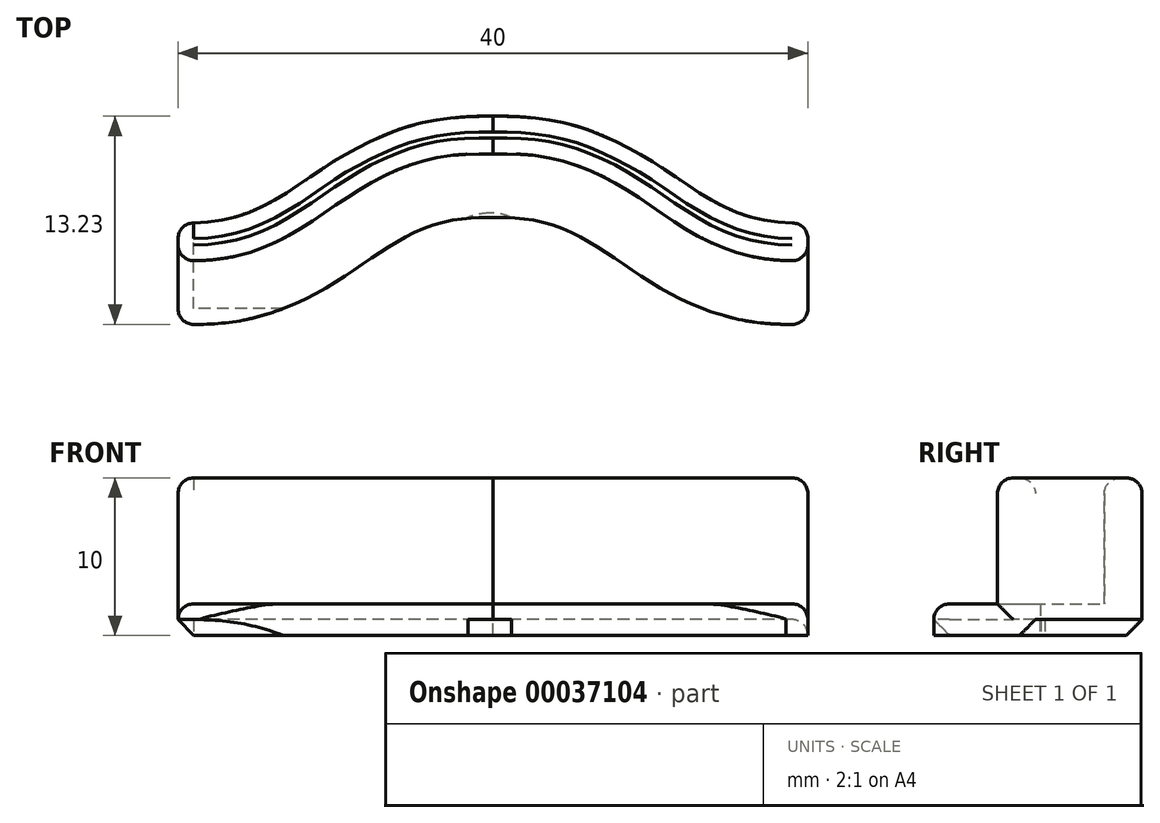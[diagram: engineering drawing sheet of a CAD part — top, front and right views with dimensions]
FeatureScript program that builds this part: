
annotation { "Feature Type Name" : "Feature", "Feature Type Description" : "" }
export const myFeature = defineFeature(function(context is Context, id is Id, definition is map)
    precondition{}
    {
        {
            var Q0;
            Q0=qCreatedBy(makeId("Top.planeOp"),FACE);
            var sketch = newSketch(context, id + "F0", { "sketchPlane" : qUnion([Q0]), "disableImprinting" : false});
            skLineSegment(sketch, "E0.bottom", {"start": v(-20, 0) * mm, "end": v(20, 0) * mm});
            skLineSegment(sketch, "E0.left", {"start": v(-20, 0) * mm, "end": v(-20, 6.45) * mm});
            skLineSegment(sketch, "E0.right", {"start": v(20, 0) * mm, "end": v(20, 6.45) * mm});
            skLineSegment(sketch, "E1", {"start": v(0, 0) * mm, "end": v(0, 13.22) * mm, "construction": true});
            skFitSpline(sketch, "E2", {"points": [v(-20, 2.4) * mm, v(0, 9.17) * mm], "startDerivative": vector(30.52, 0) * mm, "endDerivative": vector(27.9, 0) * mm});
            skFitSpline(sketch, "E3.MirrorCS", {"points": [v(20, 2.4) * mm, v(0, 9.17) * mm], "startDerivative": vector(-30.52, 0) * mm, "endDerivative": vector(-27.9, 0) * mm});
            skFitSpline(sketch, "E4.0", {"points": [v(20, 4.05) * mm, v(18.82, 4.05) * mm, v(16.78, 4.25) * mm, v(14.43, 4.95) * mm, v(12.46, 5.94) * mm, v(10.6, 7.15) * mm, v(8.63, 8.46) * mm, v(6.34, 9.7) * mm, v(3.54, 10.6) * mm, v(1.26, 10.82) * mm, v(0, 10.82) * mm]});
            skFitSpline(sketch, "E4.1", {"points": [v(-20, 4.05) * mm, v(-18.82, 4.05) * mm, v(-16.78, 4.25) * mm, v(-14.43, 4.95) * mm, v(-12.46, 5.94) * mm, v(-10.6, 7.15) * mm, v(-8.63, 8.46) * mm, v(-6.34, 9.7) * mm, v(-3.54, 10.6) * mm, v(-1.26, 10.82) * mm, v(0, 10.82) * mm]});
            skFitSpline(sketch, "E5.0", {"points": [v(20, 6.45) * mm, v(18.95, 6.45) * mm, v(17.22, 6.62) * mm, v(15.32, 7.19) * mm, v(13.69, 8) * mm, v(11.96, 9.12) * mm, v(10.24, 10.27) * mm, v(8.6, 11.2) * mm, v(6.75, 12.09) * mm, v(4.56, 12.79) * mm, v(2.06, 13.16) * mm, v(0.7, 13.22) * mm, v(0, 13.22) * mm]});
            skFitSpline(sketch, "E5.1", {"points": [v(-20, 6.45) * mm, v(-18.95, 6.45) * mm, v(-17.22, 6.62) * mm, v(-15.32, 7.19) * mm, v(-13.69, 8) * mm, v(-11.96, 9.12) * mm, v(-10.24, 10.27) * mm, v(-8.6, 11.2) * mm, v(-6.75, 12.09) * mm, v(-4.56, 12.79) * mm, v(-2.06, 13.16) * mm, v(-0.7, 13.22) * mm, v(0, 13.22) * mm]});
            skFitSpline(sketch, "E6.0", {"points": [v(20, 0) * mm, v(18.6, 0) * mm, v(16.05, 0.23) * mm, v(12.92, 1.16) * mm, v(10.38, 2.45) * mm, v(8.3, 3.8) * mm, v(6.5, 5.02) * mm, v(4.73, 5.95) * mm, v(2.74, 6.6) * mm, v(1.02, 6.77) * mm, v(0, 6.77) * mm]});
            skFitSpline(sketch, "E6.1", {"points": [v(-20, 0) * mm, v(-18.6, 0) * mm, v(-16.05, 0.23) * mm, v(-12.92, 1.16) * mm, v(-10.38, 2.45) * mm, v(-8.3, 3.8) * mm, v(-6.5, 5.02) * mm, v(-4.73, 5.95) * mm, v(-2.74, 6.6) * mm, v(-1.02, 6.77) * mm, v(0, 6.77) * mm]});
            skSolve(sketch);
        }
        {
            var Q0;
            Q0=makeQuery(id+"F0.imprint","IMPRINT",FACE,{"disambiguationData":[TD([[makeQuery(id+"F0.imprint","IMPRINT",EDGE,{"derivedFrom":sQuery(id+"F0.wireOp",EDGE,"E0.bottom")}),1.0]])]});
            var Q1;
            {var subQ3=sQuery(id+"F0.wireOp",EDGE,"E2");Q1=makeQuery(id+"F0.imprint","IMPRINT",FACE,{"disambiguationData":[TD([[makeQuery(id+"F0.imprint","IMPRINT",EDGE,{"derivedFrom":subQ3}),-1.0]])]});}
            var Q2;
            {var subQ3=sQuery(id+"F0.wireOp",EDGE,"E2");Q2=makeQuery(id+"F0.imprint","IMPRINT",FACE,{"disambiguationData":[TD([[makeQuery(id+"F0.imprint","IMPRINT",EDGE,{"derivedFrom":subQ3}),1.0]])]});}
            var Q3;
            {var subQ2=sQuery(id+"F0.wireOp",EDGE,"E4.0");Q3=makeQuery(id+"F0.imprint","IMPRINT",FACE,{"disambiguationData":[TD([[makeQuery(id+"F0.imprint","IMPRINT",EDGE,{"derivedFrom":subQ2}),-1.0]])]});}
            extrude(context, id + "F1", {"entities" : qUnion([Q0, Q1, Q2, Q3]), "depth" : 2 * mm});
        }
        {
            var Q0;
            {var subQ3=sQuery(id+"F0.wireOp",EDGE,"E2");Q0=makeQuery(id+"F0.imprint","IMPRINT",FACE,{"disambiguationData":[TD([[makeQuery(id+"F0.imprint","IMPRINT",EDGE,{"derivedFrom":subQ3}),-1.0]])]});}
            var Q1;
            {var subQ2=sQuery(id+"F0.wireOp",EDGE,"E4.0");Q1=makeQuery(id+"F0.imprint","IMPRINT",FACE,{"disambiguationData":[TD([[makeQuery(id+"F0.imprint","IMPRINT",EDGE,{"derivedFrom":subQ2}),-1.0]])]});}
            extrude(context, id + "F2", {"entities" : qUnion([Q0, Q1]), "operationType" : NewBodyOperationType.ADD, "depth" : 10 * mm});
        }
        {
            var Q0;
            Q0=makeQuery(id+"F2.opExtrude","CAP_EDGE",EDGE,{"disambiguationData":[OSD([sQuery(id+"F0.wireOp",EDGE,"E4.0")])],"isStart":false});
            var Q1;
            Q1=makeQuery(id+"F2.opExtrude","CAP_EDGE",EDGE,{"disambiguationData":[OSD([sQuery(id+"F0.wireOp",EDGE,"E4.1")])],"isStart":false});
            var Q2;
            Q2=makeQuery(id+"F2.opExtrude","CAP_EDGE",EDGE,{"disambiguationData":[OSD([sQuery(id+"F0.wireOp",EDGE,"E3.MirrorCS")])],"isStart":false});
            var Q3;
            Q3=makeQuery(id+"F2.opExtrude","SWEPT_EDGE",EDGE,{"disambiguationData":[OSD([sQuery(id+"F0.wireOp",EDGE,"E0.left"),sQuery(id+"F0.wireOp",EDGE,"E4.1")])]});
            var Q4;
            Q4=makeQuery(id+"F2.opExtrude","SWEPT_EDGE",EDGE,{"disambiguationData":[OSD([sQuery(id+"F0.wireOp",EDGE,"E0.left"),sQuery(id+"F0.wireOp",EDGE,"E2")])]});
            var Q5;
            Q5=makeQuery(id+"F2.opExtrude","SWEPT_EDGE",EDGE,{"disambiguationData":[OSD([sQuery(id+"F0.wireOp",EDGE,"E0.right"),sQuery(id+"F0.wireOp",EDGE,"E3.MirrorCS")])]});
            var Q6;
            Q6=makeQuery(id+"F2.opExtrude","SWEPT_EDGE",EDGE,{"disambiguationData":[OSD([sQuery(id+"F0.wireOp",EDGE,"E0.right"),sQuery(id+"F0.wireOp",EDGE,"E4.0")])]});
            var Q7;
            {var subQ0=sQuery(id+"F0.wireOp",EDGE,"E0.left");var subQ1=sQuery(id+"F0.wireOp",EDGE,"E5.1");Q7=makeQuery(id+"F2.boolean.opBoolean","MERGE",EDGE,{"derivedFrom":[makeQuery(id+"F1.opExtrude","SWEPT_EDGE",EDGE,{"disambiguationData":[OSD([subQ0,subQ1])]}),makeQuery(id+"F2.opExtrude","SWEPT_EDGE",EDGE,{"disambiguationData":[OSD([subQ0,subQ1])]})]});}
            var Q8;
            {var subQ0=sQuery(id+"F0.wireOp",EDGE,"E0.right");var subQ1=sQuery(id+"F0.wireOp",EDGE,"E5.0");Q8=makeQuery(id+"F2.boolean.opBoolean","MERGE",EDGE,{"derivedFrom":[makeQuery(id+"F1.opExtrude","SWEPT_EDGE",EDGE,{"disambiguationData":[OSD([subQ0,subQ1])]}),makeQuery(id+"F2.opExtrude","SWEPT_EDGE",EDGE,{"disambiguationData":[OSD([subQ0,subQ1])]})]});}
            var Q9;
            Q9=makeQuery(id+"F1.opExtrude","SWEPT_EDGE",EDGE,{"disambiguationData":[OSD([sQuery(id+"F0.wireOp",EDGE,"E0.bottom"),sQuery(id+"F0.wireOp",EDGE,"E0.left"),sQuery(id+"F0.wireOp",EDGE,"E6.1")])]});
            var Q10;
            Q10=makeQuery(id+"F1.opExtrude","SWEPT_EDGE",EDGE,{"disambiguationData":[OSD([sQuery(id+"F0.wireOp",EDGE,"E0.bottom"),sQuery(id+"F0.wireOp",EDGE,"E0.right"),sQuery(id+"F0.wireOp",EDGE,"E6.0")])]});
            var Q11;
            Q11=makeQuery(id+"F2.boolean.opBoolean","INTERSECT",EDGE,{"derivedFrom":[makeQuery(id+"F1.opExtrude","CAP_FACE",FACE,{"disambiguationData":[OSD([sQuery(id+"F0.wireOp",EDGE,"E0.bottom"),sQuery(id+"F0.wireOp",EDGE,"E0.left"),sQuery(id+"F0.wireOp",EDGE,"E0.right"),sQuery(id+"F0.wireOp",EDGE,"E5.0"),sQuery(id+"F0.wireOp",EDGE,"E5.1")])],"isStart":false}),makeQuery(id+"F2.opExtrude","SWEPT_FACE",FACE,{"disambiguationData":[OSD([sQuery(id+"F0.wireOp",EDGE,"E6.0")])]})]});
            var Q12;
            Q12=makeQuery(id+"F2.opExtrude","CAP_EDGE",EDGE,{"disambiguationData":[OSD([sQuery(id+"F0.wireOp",EDGE,"E6.1")])],"isStart":false});
            var Q13;
            Q13=makeQuery(id+"F2.opExtrude","CAP_EDGE",EDGE,{"disambiguationData":[OSD([sQuery(id+"F0.wireOp",EDGE,"E5.1")])],"isStart":false});
            var Q14;
            {var subQ0=sQuery(id+"F0.wireOp",EDGE,"E0.left");Q14=makeQuery(id+"F2.opExtrude","CAP_EDGE",EDGE,{"disambiguationData":[OSD([subQ0]),TDD([makeQuery(id+"F0.imprint","IMPRINT",EDGE,{"disambiguationData":[TD([[makeQuery(id+"F0.imprint","INTERSECT",VERTEX,{"derivedFrom":[subQ0,sQuery(id+"F0.wireOp",EDGE,"E5.1")]}),1.0]])],"derivedFrom":subQ0})])],"isStart":false});}
            var Q15;
            {var subQ0=sQuery(id+"F0.wireOp",EDGE,"E0.right");Q15=makeQuery(id+"F2.opExtrude","CAP_EDGE",EDGE,{"disambiguationData":[OSD([subQ0]),TDD([makeQuery(id+"F0.imprint","IMPRINT",EDGE,{"disambiguationData":[TD([[makeQuery(id+"F0.imprint","INTERSECT",VERTEX,{"derivedFrom":[subQ0,sQuery(id+"F0.wireOp",EDGE,"E5.0")]}),1.0]])],"derivedFrom":subQ0})])],"isStart":false});}
            var Q16;
            {var subQ0=sQuery(id+"F0.wireOp",EDGE,"E0.left");Q16=makeQuery(id+"F2.opExtrude","CAP_EDGE",EDGE,{"disambiguationData":[OSD([subQ0]),TDD([makeQuery(id+"F0.imprint","IMPRINT",EDGE,{"disambiguationData":[TD([[makeQuery(id+"F0.imprint","INTERSECT",VERTEX,{"derivedFrom":[subQ0,sQuery(id+"F0.wireOp",EDGE,"E2")]}),1.0]])],"derivedFrom":subQ0})])],"isStart":false});}
            var Q17;
            {var subQ0=sQuery(id+"F0.wireOp",EDGE,"E0.right");Q17=makeQuery(id+"F2.opExtrude","CAP_EDGE",EDGE,{"disambiguationData":[OSD([subQ0]),TDD([makeQuery(id+"F0.imprint","IMPRINT",EDGE,{"disambiguationData":[TD([[makeQuery(id+"F0.imprint","INTERSECT",VERTEX,{"derivedFrom":[subQ0,sQuery(id+"F0.wireOp",EDGE,"E3.MirrorCS")]}),1.0]])],"derivedFrom":subQ0})])],"isStart":false});}
            fillet(context, id + "F3", {"entities" : qUnion([Q0, Q1, Q2, Q3, Q4, Q5, Q6, Q7, Q8, Q9, Q10, Q11, Q12, Q13, Q14, Q15, Q16, Q17]), "radius" : 1 * mm, "tangentPropagation" : true, "allowEdgeOverflow" : false});
        }
        {
            var Q0;
            Q0=makeQuery(id+"F1.opExtrude","CAP_EDGE",EDGE,{"disambiguationData":[OSD([sQuery(id+"F0.wireOp",EDGE,"E0.bottom")])],"isStart":false});
            fillet(context, id + "F4", {"entities" : qUnion([Q0]), "radius" : 1 * mm, "tangentPropagation" : true, "allowEdgeOverflow" : false});
        }
        {
            var Q0;
            Q0=makeQuery(id+"F1.opExtrude","CAP_FACE",FACE,{"disambiguationData":[OSD([sQuery(id+"F0.wireOp",EDGE,"E0.bottom"),sQuery(id+"F0.wireOp",EDGE,"E0.left"),sQuery(id+"F0.wireOp",EDGE,"E0.right"),sQuery(id+"F0.wireOp",EDGE,"E5.0"),sQuery(id+"F0.wireOp",EDGE,"E5.1")])],"isStart":true});
            var sketch = newSketch(context, id + "F5", { "sketchPlane" : qUnion([Q0])});
            skText(sketch, "E7", { "text": "3", "fontName": "OpenSans-Bold.ttf"});
            const initialGuessF5  = {"E7": [-0.00185, -0.007, 1, 0, 0.005]};
            skSetInitialGuess(sketch, initialGuessF5);
            skSolve(sketch);
        }
        {
            var Q0;
            Q0=qSketchRegion(id+"F5",true);
            extrude(context, id + "F6", {"entities" : qUnion([Q0]), "operationType" : NewBodyOperationType.REMOVE, "oppositeDirection" : true, "depth" : 1 * mm});
        }
        {
            var Q0;
            {var subQ0=sQuery(id+"F0.wireOp",EDGE,"E5.1");var subQ1=sQuery(id+"F0.wireOp",EDGE,"E0.left");Q0=makeQuery(id+"F3.opFillet","BLEND_EDGE",EDGE,{"blendedFrom":[makeQuery(id+"F2.boolean.opBoolean","MERGE",EDGE,{"derivedFrom":[makeQuery(id+"F1.opExtrude","SWEPT_EDGE",EDGE,{"disambiguationData":[OSD([subQ1,subQ0])]}),makeQuery(id+"F2.opExtrude","SWEPT_EDGE",EDGE,{"disambiguationData":[OSD([subQ1,subQ0])]})]}),makeQuery(id+"F1.opExtrude","CAP_FACE",FACE,{"disambiguationData":[OSD([sQuery(id+"F0.wireOp",EDGE,"E0.bottom"),subQ1,sQuery(id+"F0.wireOp",EDGE,"E0.right"),sQuery(id+"F0.wireOp",EDGE,"E5.0"),subQ0])],"isStart":true})],"blendedInto":[makeQuery(id+"F1.opExtrude","CAP_FACE",FACE,{"disambiguationData":[OSD([sQuery(id+"F0.wireOp",EDGE,"E0.bottom"),subQ1,sQuery(id+"F0.wireOp",EDGE,"E0.right"),sQuery(id+"F0.wireOp",EDGE,"E5.0"),subQ0])],"isStart":true})]});}
            chamfer(context, id + "F7", {"entities" : qUnion([Q0]), "width" : 1 * mm, "tangentPropagation" : true});
        }
    });
